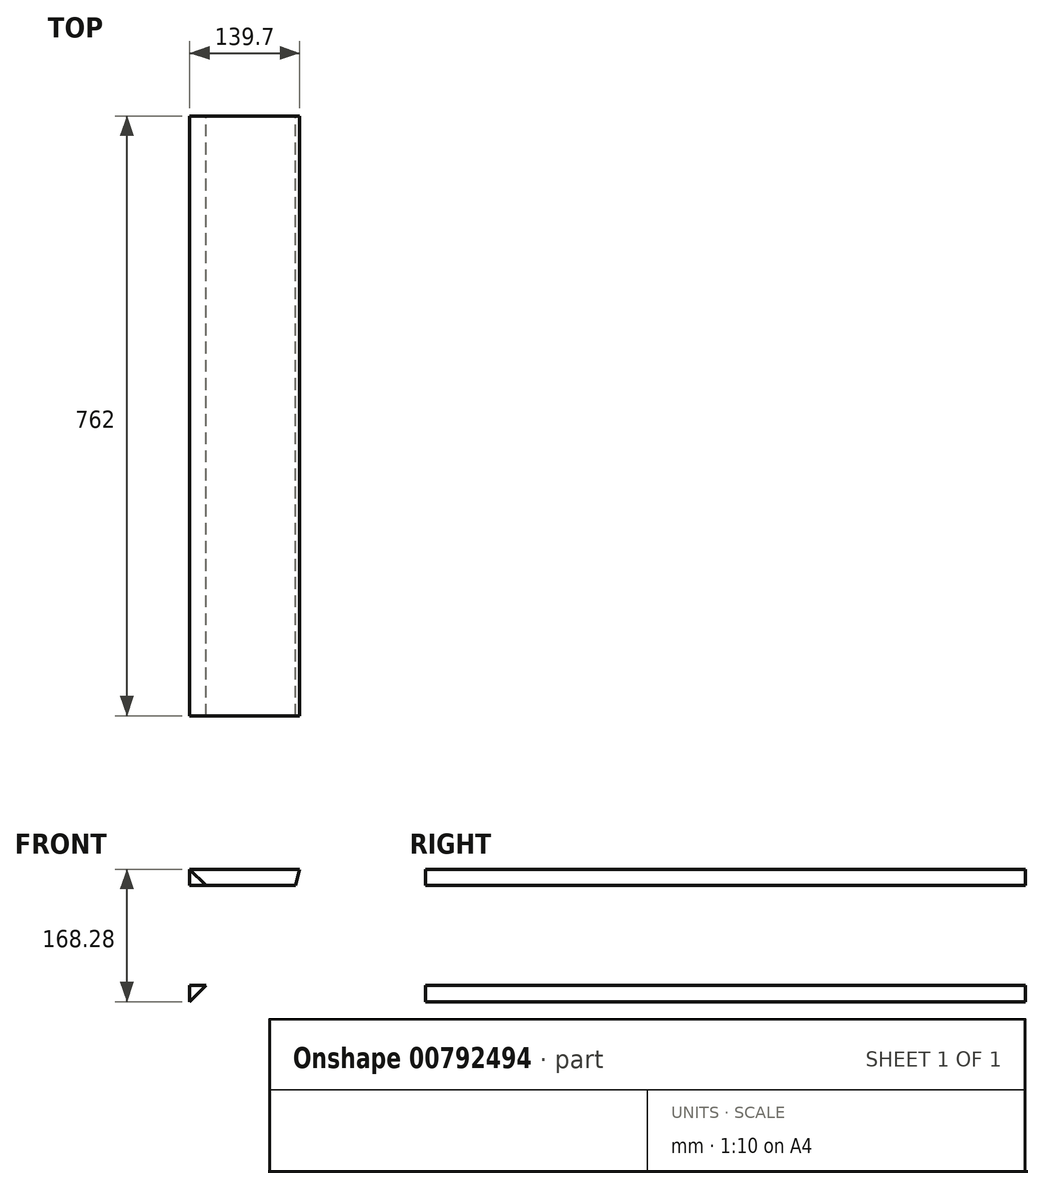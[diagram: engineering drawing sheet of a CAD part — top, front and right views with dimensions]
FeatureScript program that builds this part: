
annotation { "Feature Type Name" : "Feature", "Feature Type Description" : "" }
export const myFeature = defineFeature(function(context is Context, id is Id, definition is map)
    precondition{}
    {
        {
            var Q0;
            Q0=qCreatedBy(makeId("Front.planeOp"),FACE);
            var sketch = newSketch(context, id + "F0", { "sketchPlane" : qUnion([Q0])});
            skLineSegment(sketch, "E0.bottom", {"start": v(0, 0) * mm, "end": v(103.19, 0) * mm});
            skLineSegment(sketch, "E0.top", {"start": v(0, 20.64) * mm, "end": v(103.19, 20.64) * mm});
            skLineSegment(sketch, "E0.left", {"start": v(0, 0) * mm, "end": v(0, 20.64) * mm});
            skLineSegment(sketch, "E0.right", {"start": v(103.19, 0) * mm, "end": v(103.19, 20.64) * mm, "construction": true});
            skLineSegment(sketch, "E1.bottom", {"start": v(0, 20.64) * mm, "end": v(20.64, 20.64) * mm});
            skLineSegment(sketch, "E1.top", {"start": v(0, 147.64) * mm, "end": v(20.64, 147.64) * mm});
            skLineSegment(sketch, "E1.left", {"start": v(0, 20.64) * mm, "end": v(0, 147.64) * mm});
            skLineSegment(sketch, "E1.right", {"start": v(20.64, 20.64) * mm, "end": v(20.64, 147.64) * mm});
            skLineSegment(sketch, "E2.bottom", {"start": v(0, 147.64) * mm, "end": v(139.7, 147.64) * mm});
            skLineSegment(sketch, "E2.top", {"start": v(0, 168.28) * mm, "end": v(139.7, 168.28) * mm});
            skLineSegment(sketch, "E2.left", {"start": v(0, 147.64) * mm, "end": v(0, 168.28) * mm});
            skLineSegment(sketch, "E2.right", {"start": v(139.7, 147.64) * mm, "end": v(139.7, 168.28) * mm, "construction": true});
            skLineSegment(sketch, "E3", {"start": v(139.7, 168.28) * mm, "end": v(98.08, 0) * mm});
            skLineSegment(sketch, "E4", {"start": v(0, 168.28) * mm, "end": v(20.64, 147.64) * mm});
            skLineSegment(sketch, "E5", {"start": v(20.64, 20.64) * mm, "end": v(0, 0) * mm});
            skSolve(sketch);
        }
        {
            var Q0;
            {var subQ1=sQuery(id+"F0.wireOp",EDGE,"E2.top");Q0=makeQuery(id+"F0.imprint","IMPRINT",FACE,{"disambiguationData":[TD([[makeQuery(id+"F0.imprint","IMPRINT",EDGE,{"derivedFrom":subQ1}),-1.0]])]});}
            var Q1;
            {var subQ1=sQuery(id+"F0.wireOp",EDGE,"E0.top");Q1=makeQuery(id+"F0.imprint","IMPRINT",FACE,{"disambiguationData":[TD([[makeQuery(id+"F0.imprint","IMPRINT",EDGE,{"derivedFrom":subQ1}),-1.0]])]});}
            extrude(context, id + "F1", {"entities" : qUnion([Q0, Q1]), "depth" : 762 * mm, "offsetDistance" : 25.4 * mm});
        }
        {
            var Q0;
            {var subQ0=sQuery(id+"F0.wireOp",EDGE,"E2.left");Q0=makeQuery(id+"F0.imprint","IMPRINT",FACE,{"disambiguationData":[TD([[makeQuery(id+"F0.imprint","IMPRINT",EDGE,{"derivedFrom":subQ0}),-1.0]])]});}
            var Q1;
            Q1=makeQuery(id+"F0.imprint","IMPRINT",FACE,{"disambiguationData":[TD([[makeQuery(id+"F0.imprint","IMPRINT",EDGE,{"derivedFrom":sQuery(id+"F0.wireOp",EDGE,"E1.bottom")}),1.0]])]});
            var Q2;
            Q2=makeQuery(id+"F0.imprint","IMPRINT",FACE,{"disambiguationData":[TD([[makeQuery(id+"F0.imprint","IMPRINT",EDGE,{"derivedFrom":sQuery(id+"F0.wireOp",EDGE,"E0.left")}),-1.0]])]});
            var Q3;
            Q3=makeQuery(id+"F1.opExtrude","CAP_FACE",FACE,{"disambiguationData":[OSD([sQuery(id+"F0.wireOp",EDGE,"E2.bottom"),sQuery(id+"F0.wireOp",EDGE,"E2.top"),sQuery(id+"F0.wireOp",EDGE,"E3"),sQuery(id+"F0.wireOp",EDGE,"E4")])],"isStart":false});
            extrude(context, id + "F2", {"entities" : qUnion([Q0, Q1, Q2]), "endBound" : BoundingType.UP_TO_SURFACE, "depth" : 25.4 * mm, "endBoundEntityFace" : qUnion([Q3]), "offsetDistance" : 25.4 * mm});
        }
    });
